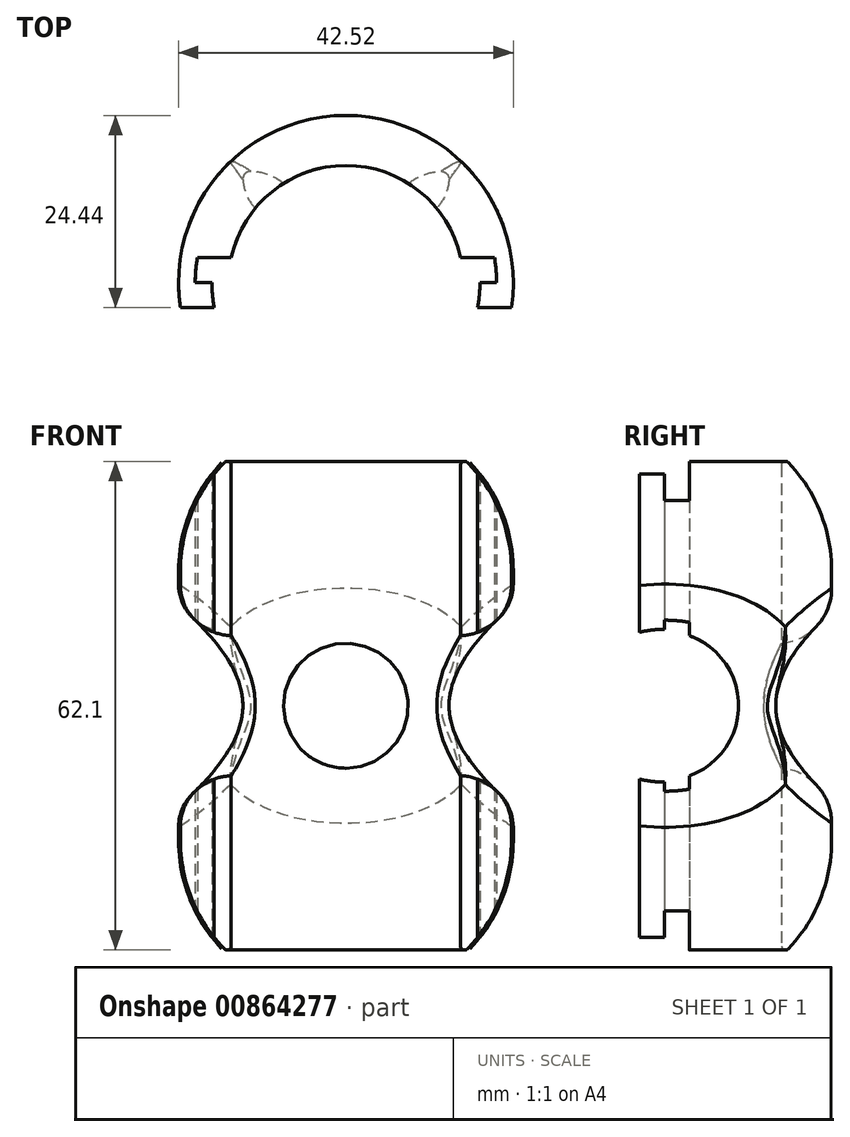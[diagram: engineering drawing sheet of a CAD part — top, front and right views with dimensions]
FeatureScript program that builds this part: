
annotation { "Feature Type Name" : "Feature", "Feature Type Description" : "" }
export const myFeature = defineFeature(function(context is Context, id is Id, definition is map)
    precondition{}
    {
        {
            var Q0;
            Q0=qCreatedBy(makeId("Top.planeOp"),FACE);
            var sketch = newSketch(context, id + "F0", { "sketchPlane" : qUnion([Q0])});
            skArc(sketch, "E0", {"start": v(21.02, 3.18) * mm, "mid": v(0, 21.26) * mm, "end": v(-21.02, 3.18) * mm});
            skLineSegment(sketch, "E1", {"start": v(-25.03, 0) * mm, "end": v(-21.26, 0) * mm, "construction": true});
            skLineSegment(sketch, "E2.top", {"start": v(-25.03, 3.17) * mm, "end": v(-21.02, 3.17) * mm, "construction": true});
            skLineSegment(sketch, "E2.left", {"start": v(-25.03, 0) * mm, "end": v(-25.03, 3.17) * mm, "construction": true});
            skLineSegment(sketch, "E2.right", {"start": v(24.88, 0) * mm, "end": v(24.88, 3.17) * mm, "construction": true});
            skLineSegment(sketch, "E3.top", {"start": v(-25.03, -3.17) * mm, "end": v(-21.02, -3.17) * mm, "construction": true});
            skLineSegment(sketch, "E3.left", {"start": v(-25.03, 0) * mm, "end": v(-25.03, -3.17) * mm, "construction": true});
            skLineSegment(sketch, "E3.right", {"start": v(24.88, 0) * mm, "end": v(24.88, -3.17) * mm, "construction": true});
            skLineSegment(sketch, "E4", {"start": v(-18.88, -3.17) * mm, "end": v(-16.73, -3.17) * mm});
            skLineSegment(sketch, "E5", {"start": v(-17.02, 0) * mm, "end": v(-19.14, 0) * mm});
            skLineSegment(sketch, "E6", {"start": v(14.56, -3.17) * mm, "end": v(18.88, -3.17) * mm});
            skLineSegment(sketch, "E7", {"start": v(19.14, 0) * mm, "end": v(17.02, 0) * mm});
            skLineSegment(sketch, "E8.trimOffspring", {"start": v(21.26, 0) * mm, "end": v(24.88, 0) * mm, "construction": true});
            skArc(sketch, "E9.trimOffspring", {"start": v(14.56, 3.18) * mm, "mid": v(0, 14.9) * mm, "end": v(-14.56, 3.17) * mm});
            skLineSegment(sketch, "E10.trimOffspring", {"start": v(16.73, -3.17) * mm, "end": v(18.88, -3.17) * mm, "construction": true});
            skLineSegment(sketch, "E11.trimOffspring", {"start": v(21.02, 3.17) * mm, "end": v(24.88, 3.17) * mm, "construction": true});
            skLineSegment(sketch, "E12", {"start": v(-14.56, -3.17) * mm, "end": v(-16.73, -3.17) * mm});
            skLineSegment(sketch, "E13.trimOffspring", {"start": v(-18.88, -3.17) * mm, "end": v(14.56, -3.17) * mm, "construction": true});
            skLineSegment(sketch, "E14.trimOffspring", {"start": v(-14.56, 3.17) * mm, "end": v(14.56, 3.17) * mm, "construction": true});
            skLineSegment(sketch, "E15.trimOffspring", {"start": v(-14.9, 0) * mm, "end": v(14.9, 0) * mm, "construction": true});
            skLineSegment(sketch, "E16.trimOffspring", {"start": v(17.02, 0) * mm, "end": v(19.14, 0) * mm, "construction": true});
            skLineSegment(sketch, "E17.trimOffspring", {"start": v(21.02, -3.17) * mm, "end": v(24.88, -3.17) * mm, "construction": true});
            skLineSegment(sketch, "E18", {"start": v(-18.88, 3.18) * mm, "end": v(-16.73, 3.17) * mm});
            skLineSegment(sketch, "E19", {"start": v(16.73, 3.17) * mm, "end": v(18.88, 3.17) * mm});
            skArc(sketch, "E20", {"start": v(-19.14, 0) * mm, "mid": v(-19.07, 1.6) * mm, "end": v(-18.88, 3.18) * mm});
            skArc(sketch, "E21", {"start": v(-21.02, 3.18) * mm, "mid": v(-21.26, 0) * mm, "end": v(-21.02, -3.17) * mm});
            skArc(sketch, "E22", {"start": v(-16.73, -3.17) * mm, "mid": v(-16.95, -1.6) * mm, "end": v(-17.02, 0) * mm});
            skArc(sketch, "E23", {"start": v(18.88, 3.17) * mm, "mid": v(19.07, 1.6) * mm, "end": v(19.14, 0) * mm});
            skArc(sketch, "E24", {"start": v(21.02, 3.18) * mm, "mid": v(21.26, 0) * mm, "end": v(21.02, -3.18) * mm});
            skLineSegment(sketch, "E25", {"start": v(-21.02, -3.17) * mm, "end": v(-18.88, -3.17) * mm});
            skLineSegment(sketch, "E26", {"start": v(18.88, -3.17) * mm, "end": v(21.02, -3.17) * mm});
            skArc(sketch, "E27.trimOffspring", {"start": v(17.02, 0) * mm, "mid": v(16.95, -1.6) * mm, "end": v(16.73, -3.17) * mm});
            skLineSegment(sketch, "E28", {"start": v(14.56, 3.17) * mm, "end": v(16.73, 3.17) * mm});
            skLineSegment(sketch, "E29", {"start": v(-14.56, 3.18) * mm, "end": v(-16.73, 3.17) * mm});
            skLineSegment(sketch, "E30", {"start": v(-14.9, 0) * mm, "end": v(-17.02, 0) * mm});
            skLineSegment(sketch, "E31.trimOffspring", {"start": v(-19.14, 0) * mm, "end": v(-17.02, 0) * mm, "construction": true});
            skSolve(sketch);
        }
        {
            var Q0;
            {var subQ5=sQuery(id+"F0.wireOp",EDGE,"E0");Q0=makeQuery(id+"F0.imprint","IMPRINT",FACE,{"disambiguationData":[TD([[makeQuery(id+"F0.imprint","IMPRINT",EDGE,{"derivedFrom":subQ5}),1.0]])]});}
            var Q1;
            {var subQ0=sQuery(id+"F0.wireOp",EDGE,"pCsfrZGq-e50Y-0pSW-2guC-nt5aPkTz24II");var subQ1=sQuery(id+"F0.wireOp",EDGE,"nqwLaSXD-lHEw-VPrE-TKFq-Z4Lxf12zn3U3");var subQ2=makeQuery(id+"F0.imprint","INTERSECT",VERTEX,{"derivedFrom":[subQ1,subQ0]});Q1=makeQuery(id+"F0.imprint","IMPRINT",FACE,{"disambiguationData":[TD([[makeQuery(id+"F0.imprint","IMPRINT",EDGE,{"disambiguationData":[TD([[subQ2,1.0]])],"derivedFrom":subQ1}),-1.0]])]});}
            var Q2;
            {var subQ7=sQuery(id+"F0.wireOp",EDGE,"8c7SRqRP-1X77-zhYG-Pu1Q-lgxM2d8JSe8a");Q2=makeQuery(id+"F0.imprint","IMPRINT",FACE,{"disambiguationData":[TD([[makeQuery(id+"F0.imprint","IMPRINT",EDGE,{"derivedFrom":subQ7}),-1.0]])]});}
            var Q3;
            {var subQ4=sQuery(id+"F0.wireOp",EDGE,"E5");Q3=makeQuery(id+"F0.imprint","IMPRINT",FACE,{"disambiguationData":[TD([[makeQuery(id+"F0.imprint","IMPRINT",EDGE,{"derivedFrom":subQ4}),1.0]])]});}
            var Q4;
            {var subQ4=sQuery(id+"F0.wireOp",EDGE,"edyOfBYv-rt52-n9m8-jdVz-S8zG1rsjcPio");Q4=makeQuery(id+"F0.imprint","IMPRINT",FACE,{"disambiguationData":[TD([[makeQuery(id+"F0.imprint","IMPRINT",EDGE,{"derivedFrom":subQ4}),1.0]])]});}
            extrude(context, id + "F1", {"entities" : qUnion([Q0, Q1, Q2, Q3, Q4]), "depth" : 63.5 * mm, "offsetDistance" : 25 * mm});
        }
        {
            var Q0;
            Q0=qCreatedBy(makeId("Front.planeOp"),FACE);
            var sketch = newSketch(context, id + "F2", { "sketchPlane" : qUnion([Q0])});
            skLineSegment(sketch, "E32", {"start": v(0, 0) * mm, "end": v(0, 31.75) * mm, "construction": true});
            skCircle(sketch, "E33", {"center": v(0, 31.75) * mm, "radius": 7.94 * mm});
            skSolve(sketch);
        }
        {
            var Q0;
            Q0=makeQuery(id+"F2.imprint","IMPRINT",FACE,{"disambiguationData":[TD([[makeQuery(id+"F2.imprint","IMPRINT",EDGE,{"derivedFrom":sQuery(id+"F2.wireOp",EDGE,"E33")}),1.0]])]});
            extrude(context, id + "F3", {"entities" : qUnion([Q0]), "operationType" : NewBodyOperationType.REMOVE, "endBound" : BoundingType.THROUGH_ALL, "oppositeDirection" : true, "depth" : 25 * mm, "offsetDistance" : 25 * mm});
        }
        {
            var Q0;
            Q0=qCreatedBy(makeId("Right.planeOp"),FACE);
            var sketch = newSketch(context, id + "F4", { "sketchPlane" : qUnion([Q0])});
            skLineSegment(sketch, "E34", {"start": v(0, 0) * mm, "end": v(0, 0) * mm});
            skLineSegment(sketch, "E35", {"start": v(0, 0) * mm, "end": v(0, 31.75) * mm, "construction": true});
            skCircle(sketch, "E36", {"center": v(0, 31.75) * mm, "radius": 9.45 * mm});
            skSolve(sketch);
        }
        {
            var Q0;
            Q0=makeQuery(id+"F4.imprint","IMPRINT",FACE,{"disambiguationData":[TD([[makeQuery(id+"F4.imprint","IMPRINT",EDGE,{"derivedFrom":sQuery(id+"F4.wireOp",EDGE,"E36")}),1.0]])]});
            extrude(context, id + "F5", {"entities" : qUnion([Q0]), "operationType" : NewBodyOperationType.REMOVE, "endBound" : BoundingType.THROUGH_ALL, "oppositeDirection" : true, "depth" : 25 * mm, "offsetDistance" : 25 * mm, "hasSecondDirection" : true, "secondDirectionBound" : SecondDirectionBoundingType.THROUGH_ALL, "secondDirectionOppositeDirection" : false, "secondDirectionDepth" : 25 * mm});
        }
        {
            var Q0;
            Q0=makeQuery(id+"F1.opExtrude","CAP_EDGE",EDGE,{"disambiguationData":[OSD([sQuery(id+"F0.wireOp",EDGE,"E0")])],"isStart":false});
            var Q1;
            Q1=makeQuery(id+"F1.opExtrude","CAP_EDGE",EDGE,{"disambiguationData":[OSD([sQuery(id+"F0.wireOp",EDGE,"E0")])],"isStart":true});
            fillet(context, id + "F6", {"entities" : qUnion([Q0, Q1]), "radius" : 20 * mm, "tangentPropagation" : true, "allowEdgeOverflow" : false});
        }
        {
            var Q0;
            Q0=makeQuery(id+"F3.boolean.opBoolean","INTERSECT",EDGE,{"derivedFrom":[makeQuery(id+"F1.opExtrude","SWEPT_FACE",FACE,{"disambiguationData":[OSD([sQuery(id+"F0.wireOp",EDGE,"E0")])]}),makeQuery(id+"F3.opExtrude","SWEPT_FACE",FACE,{"disambiguationData":[OSD([sQuery(id+"F2.wireOp",EDGE,"E33")])]})]});
            fillet(context, id + "F7", {"entities" : qUnion([Q0]), "radius" : 7 * mm, "tangentPropagation" : true, "allowEdgeOverflow" : false});
        }
        {
            var Q0;
            Q0=makeQuery(id+"F5.boolean.opBoolean","INTERSECT",EDGE,{"disambiguationData":[OD(0.0)],"derivedFrom":[makeQuery(id+"F1.opExtrude","SWEPT_FACE",FACE,{"disambiguationData":[OSD([sQuery(id+"F0.wireOp",EDGE,"E0")])]}),makeQuery(id+"F5.opExtrude","SWEPT_FACE",FACE,{"disambiguationData":[OSD([sQuery(id+"F4.wireOp",EDGE,"E36")])]})]});
            var Q1;
            Q1=makeQuery(id+"F5.boolean.opBoolean","INTERSECT",EDGE,{"disambiguationData":[OD(1.0)],"derivedFrom":[makeQuery(id+"F1.opExtrude","SWEPT_FACE",FACE,{"disambiguationData":[OSD([sQuery(id+"F0.wireOp",EDGE,"E0")])]}),makeQuery(id+"F5.opExtrude","SWEPT_FACE",FACE,{"disambiguationData":[OSD([sQuery(id+"F4.wireOp",EDGE,"E36")])]})]});
            var Q2;
            Q2=makeQuery(id+"F5.boolean.opBoolean","INTERSECT",EDGE,{"disambiguationData":[OD(0.0)],"derivedFrom":[makeQuery(id+"F1.opExtrude","SWEPT_FACE",FACE,{"disambiguationData":[OSD([sQuery(id+"F0.wireOp",EDGE,"edyOfBYv-rt52-n9m8-jdVz-S8zG1rsjcPio")])]}),makeQuery(id+"F5.opExtrude","SWEPT_FACE",FACE,{"disambiguationData":[OSD([sQuery(id+"F4.wireOp",EDGE,"E36")])]})]});
            var Q3;
            Q3=makeQuery(id+"F5.boolean.opBoolean","INTERSECT",EDGE,{"disambiguationData":[OD(1.0)],"derivedFrom":[makeQuery(id+"F1.opExtrude","SWEPT_FACE",FACE,{"disambiguationData":[OSD([sQuery(id+"F0.wireOp",EDGE,"edyOfBYv-rt52-n9m8-jdVz-S8zG1rsjcPio")])]}),makeQuery(id+"F5.opExtrude","SWEPT_FACE",FACE,{"disambiguationData":[OSD([sQuery(id+"F4.wireOp",EDGE,"E36")])]})]});
            fillet(context, id + "F8", {"entities" : qUnion([Q0, Q1, Q2, Q3]), "radius" : 6 * mm, "tangentPropagation" : true, "allowEdgeOverflow" : false});
        }
        {
            var Q0;
            {var subQ0=sQuery(id+"F0.wireOp",EDGE,"E24");var subQ1=sQuery(id+"F0.wireOp",EDGE,"E21");var subQ2=sQuery(id+"F0.wireOp",EDGE,"E0");Q0=makeQuery(id+"F8.opFillet","BLEND_EDGE",EDGE,{"blendedFrom":[makeQuery(id+"F5.boolean.opBoolean","INTERSECT",EDGE,{"disambiguationData":[OD(1.0)],"derivedFrom":[makeQuery(id+"F1.opExtrude","SWEPT_FACE",FACE,{"disambiguationData":[OSD([subQ2,subQ1,subQ0])]}),makeQuery(id+"F5.opExtrude","SWEPT_FACE",FACE,{"disambiguationData":[OSD([sQuery(id+"F4.wireOp",EDGE,"E36")])]})]}),makeQuery(id+"F7.opFillet","BLEND_FACE",FACE,{"disambiguationData":[OSD([subQ2,subQ1,subQ0,sQuery(id+"F2.wireOp",EDGE,"E33")])]})],"blendedInto":[makeQuery(id+"F7.opFillet","BLEND_FACE",FACE,{"disambiguationData":[OSD([subQ2,subQ1,subQ0,sQuery(id+"F2.wireOp",EDGE,"E33")])]})]});}
            var Q1;
            {var subQ0=sQuery(id+"F0.wireOp",EDGE,"E24");var subQ1=sQuery(id+"F0.wireOp",EDGE,"E21");var subQ2=sQuery(id+"F0.wireOp",EDGE,"E0");Q1=makeQuery(id+"F8.opFillet","BLEND_EDGE",EDGE,{"blendedFrom":[makeQuery(id+"F5.boolean.opBoolean","INTERSECT",EDGE,{"disambiguationData":[OD(0.0)],"derivedFrom":[makeQuery(id+"F1.opExtrude","SWEPT_FACE",FACE,{"disambiguationData":[OSD([subQ2,subQ1,subQ0])]}),makeQuery(id+"F5.opExtrude","SWEPT_FACE",FACE,{"disambiguationData":[OSD([sQuery(id+"F4.wireOp",EDGE,"E36")])]})]}),makeQuery(id+"F7.opFillet","BLEND_FACE",FACE,{"disambiguationData":[OSD([subQ2,subQ1,subQ0,sQuery(id+"F2.wireOp",EDGE,"E33")])]})],"blendedInto":[makeQuery(id+"F7.opFillet","BLEND_FACE",FACE,{"disambiguationData":[OSD([subQ2,subQ1,subQ0,sQuery(id+"F2.wireOp",EDGE,"E33")])]})]});}
            fillet(context, id + "F9", {"entities" : qUnion([Q0, Q1]), "radius" : 1 * mm, "tangentPropagation" : true, "allowEdgeOverflow" : false});
        }
        {
            var Q0;
            Q0=makeQuery(id+"F6.opFillet","BLEND_EDGE",EDGE,{"blendedFrom":[makeQuery(id+"F1.opExtrude","CAP_EDGE",EDGE,{"disambiguationData":[OSD([sQuery(id+"F0.wireOp",EDGE,"E0"),sQuery(id+"F0.wireOp",EDGE,"E21"),sQuery(id+"F0.wireOp",EDGE,"E24")])],"isStart":false}),makeQuery(id+"F1.opExtrude","SWEPT_FACE",FACE,{"disambiguationData":[OSD([sQuery(id+"F0.wireOp",EDGE,"E9.trimOffspring")])]})],"blendedInto":[makeQuery(id+"F1.opExtrude","SWEPT_FACE",FACE,{"disambiguationData":[OSD([sQuery(id+"F0.wireOp",EDGE,"E9.trimOffspring")])]})]});
            var Q1;
            Q1=makeQuery(id+"F6.opFillet","BLEND_EDGE",EDGE,{"blendedFrom":[makeQuery(id+"F1.opExtrude","CAP_EDGE",EDGE,{"disambiguationData":[OSD([sQuery(id+"F0.wireOp",EDGE,"E0"),sQuery(id+"F0.wireOp",EDGE,"E21"),sQuery(id+"F0.wireOp",EDGE,"E24")])],"isStart":true}),makeQuery(id+"F1.opExtrude","SWEPT_FACE",FACE,{"disambiguationData":[OSD([sQuery(id+"F0.wireOp",EDGE,"E9.trimOffspring")])]})],"blendedInto":[makeQuery(id+"F1.opExtrude","SWEPT_FACE",FACE,{"disambiguationData":[OSD([sQuery(id+"F0.wireOp",EDGE,"E9.trimOffspring")])]})]});
            fillet(context, id + "F10", {"entities" : qUnion([Q0, Q1]), "radius" : .5 * mm, "tangentPropagation" : true, "allowEdgeOverflow" : false});
        }
    });
